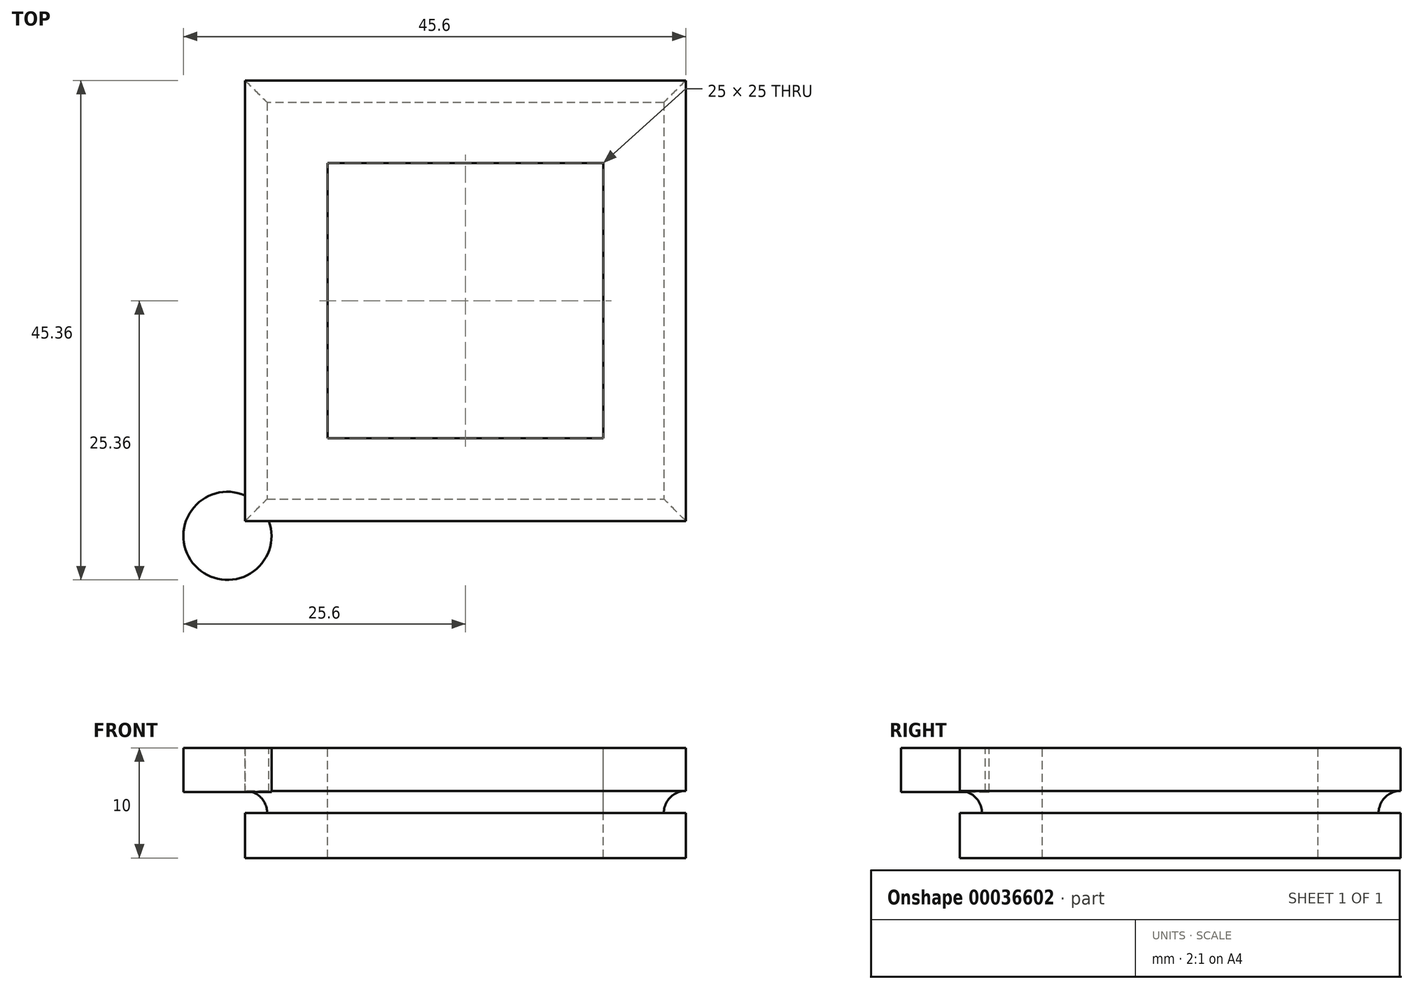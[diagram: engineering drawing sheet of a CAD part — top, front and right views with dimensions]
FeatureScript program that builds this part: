
annotation { "Feature Type Name" : "Feature", "Feature Type Description" : "" }
export const myFeature = defineFeature(function(context is Context, id is Id, definition is map)
    precondition{}
    {
        {
            var Q0;
            Q0=qCreatedBy(makeId("Top.planeOp"),FACE);
            var sketch = newSketch(context, id + "F0", { "sketchPlane" : qUnion([Q0])});
            skLineSegment(sketch, "E0.rect.bottom", {"start": v(-20, -20) * mm, "end": v(20, -20) * mm});
            skLineSegment(sketch, "E0.rect.top", {"start": v(-20, 20) * mm, "end": v(20, 20) * mm});
            skLineSegment(sketch, "E0.rect.left", {"start": v(-20, -20) * mm, "end": v(-20, 20) * mm});
            skLineSegment(sketch, "E0.rect.right", {"start": v(20, -20) * mm, "end": v(20, 20) * mm});
            skPoint(sketch, "E0.rect.middle", {"position": v(0, 0) * mm});
            skSolve(sketch);
        }
        {
            var Q0;
            Q0=makeQuery(id+"F0.imprint","IMPRINT",FACE,{"disambiguationData":[TD([[makeQuery(id+"F0.imprint","IMPRINT",EDGE,{"derivedFrom":sQuery(id+"F0.wireOp",EDGE,"E0.rect.bottom")}),1.0]])]});
            extrude(context, id + "F1", {"entities" : qUnion([Q0]), "depth" : 10 * mm});
        }
        {
            var Q0;
            Q0=makeQuery(id+"F1.opExtrude","CAP_FACE",FACE,{"disambiguationData":[OSD([sQuery(id+"F0.wireOp",EDGE,"E0.rect.bottom"),sQuery(id+"F0.wireOp",EDGE,"E0.rect.top"),sQuery(id+"F0.wireOp",EDGE,"E0.rect.left"),sQuery(id+"F0.wireOp",EDGE,"E0.rect.right")])],"isStart":false});
            var sketch = newSketch(context, id + "F2", { "sketchPlane" : qUnion([Q0])});
            skLineSegment(sketch, "E1.rect.bottom", {"start": v(-12.5, 12.5) * mm, "end": v(12.5, 12.5) * mm});
            skLineSegment(sketch, "E1.rect.top", {"start": v(-12.5, -12.5) * mm, "end": v(12.5, -12.5) * mm});
            skLineSegment(sketch, "E1.rect.left", {"start": v(-12.5, 12.5) * mm, "end": v(-12.5, -12.5) * mm});
            skLineSegment(sketch, "E1.rect.right", {"start": v(12.5, 12.5) * mm, "end": v(12.5, -12.5) * mm});
            skPoint(sketch, "E1.rect.middle", {"position": v(0, 0) * mm});
            skSolve(sketch);
        }
        {
            var Q0;
            Q0=makeQuery(id+"F2.imprint","IMPRINT",FACE,{"disambiguationData":[TD([[makeQuery(id+"F2.imprint","IMPRINT",EDGE,{"derivedFrom":sQuery(id+"F2.wireOp",EDGE,"E1.rect.bottom")}),-1.0]])]});
            extrude(context, id + "F3", {"entities" : qUnion([Q0]), "operationType" : NewBodyOperationType.REMOVE, "oppositeDirection" : true, "depth" : 10 * mm});
        }
        {
            var Q0;
            Q0=makeQuery(id+"F1.opExtrude","SWEPT_FACE",FACE,{"disambiguationData":[OSD([sQuery(id+"F0.wireOp",EDGE,"E0.rect.bottom")])]});
            var sketch = newSketch(context, id + "F4", { "sketchPlane" : qUnion([Q0])});
            skLineSegment(sketch, "E2.bottom", {"start": v(-20, 6.1) * mm, "end": v(20, 6.1) * mm});
            skLineSegment(sketch, "E2.top", {"start": v(-20, 4.1) * mm, "end": v(20, 4.1) * mm});
            skLineSegment(sketch, "E2.left", {"start": v(-20, 6.1) * mm, "end": v(-20, 4.1) * mm});
            skLineSegment(sketch, "E2.right", {"start": v(20, 6.1) * mm, "end": v(20, 4.1) * mm});
            skSolve(sketch);
        }
        {
            var Q0;
            Q0=makeQuery(id+"F4.imprint","IMPRINT",FACE,{"disambiguationData":[TD([[makeQuery(id+"F4.imprint","IMPRINT",EDGE,{"derivedFrom":sQuery(id+"F4.wireOp",EDGE,"E2.bottom")}),-1.0]])]});
            extrude(context, id + "F5", {"entities" : qUnion([Q0]), "operationType" : NewBodyOperationType.REMOVE, "oppositeDirection" : true, "depth" : 2 * mm});
        }
        {
            var Q0;
            Q0=makeQuery(id+"F1.opExtrude","SWEPT_FACE",FACE,{"disambiguationData":[OSD([sQuery(id+"F0.wireOp",EDGE,"E0.rect.right")])]});
            var sketch = newSketch(context, id + "F6", { "sketchPlane" : qUnion([Q0])});
            skLineSegment(sketch, "E3.bottom", {"start": v(-18, 6.1) * mm, "end": v(20, 6.1) * mm});
            skLineSegment(sketch, "E3.top", {"start": v(-18, 4.1) * mm, "end": v(20, 4.1) * mm});
            skLineSegment(sketch, "E3.left", {"start": v(-18, 6.1) * mm, "end": v(-18, 4.1) * mm});
            skLineSegment(sketch, "E3.right", {"start": v(20, 6.1) * mm, "end": v(20, 4.1) * mm});
            skSolve(sketch);
        }
        {
            var Q0;
            Q0=makeQuery(id+"F6.imprint","IMPRINT",FACE,{"disambiguationData":[TD([[makeQuery(id+"F6.imprint","IMPRINT",EDGE,{"derivedFrom":sQuery(id+"F6.wireOp",EDGE,"E3.bottom")}),-1.0]])]});
            extrude(context, id + "F7", {"entities" : qUnion([Q0]), "operationType" : NewBodyOperationType.REMOVE, "oppositeDirection" : true, "depth" : 2 * mm});
        }
        {
            var Q0;
            Q0=makeQuery(id+"F1.opExtrude","SWEPT_FACE",FACE,{"disambiguationData":[OSD([sQuery(id+"F0.wireOp",EDGE,"E0.rect.top")])]});
            var sketch = newSketch(context, id + "F8", { "sketchPlane" : qUnion([Q0])});
            skLineSegment(sketch, "E4.bottom", {"start": v(-18, 6.1) * mm, "end": v(20, 6.1) * mm});
            skLineSegment(sketch, "E4.top", {"start": v(-18, 4.1) * mm, "end": v(20, 4.1) * mm});
            skLineSegment(sketch, "E4.left", {"start": v(-18, 6.1) * mm, "end": v(-18, 4.1) * mm});
            skLineSegment(sketch, "E4.right", {"start": v(20, 6.1) * mm, "end": v(20, 4.1) * mm});
            skSolve(sketch);
        }
        {
            var Q0;
            {var subQ5=sQuery(id+"F8.wireOp",EDGE,"E4.bottom");Q0=makeQuery(id+"F8.imprint","IMPRINT",FACE,{"disambiguationData":[TD([[makeQuery(id+"F8.imprint","IMPRINT",EDGE,{"derivedFrom":subQ5}),-1.0]])]});}
            extrude(context, id + "F9", {"entities" : qUnion([Q0]), "operationType" : NewBodyOperationType.REMOVE, "oppositeDirection" : true, "depth" : 2 * mm});
        }
        {
            var Q0;
            Q0=makeQuery(id+"F1.opExtrude","SWEPT_FACE",FACE,{"disambiguationData":[OSD([sQuery(id+"F0.wireOp",EDGE,"E0.rect.left")])]});
            var sketch = newSketch(context, id + "F10", { "sketchPlane" : qUnion([Q0])});
            skLineSegment(sketch, "E5.bottom", {"start": v(-18, 6.1) * mm, "end": v(18, 6.1) * mm});
            skLineSegment(sketch, "E5.top", {"start": v(-18, 4.1) * mm, "end": v(18, 4.1) * mm});
            skLineSegment(sketch, "E5.left", {"start": v(-18, 6.1) * mm, "end": v(-18, 4.1) * mm});
            skLineSegment(sketch, "E5.right", {"start": v(18, 6.1) * mm, "end": v(18, 4.1) * mm});
            skSolve(sketch);
        }
        {
            var Q0;
            Q0=makeQuery(id+"F10.imprint","IMPRINT",FACE,{"disambiguationData":[TD([[makeQuery(id+"F10.imprint","IMPRINT",EDGE,{"derivedFrom":sQuery(id+"F10.wireOp",EDGE,"E5.bottom")}),-1.0]])]});
            extrude(context, id + "F11", {"entities" : qUnion([Q0]), "operationType" : NewBodyOperationType.REMOVE, "oppositeDirection" : true, "depth" : 2 * mm});
        }
        {
            var Q0;
            Q0=makeQuery(id+"F7.boolean.opBoolean","COPY",EDGE,{"derivedFrom":makeQuery(id+"F7.opExtrude","CAP_EDGE",EDGE,{"disambiguationData":[OSD([sQuery(id+"F6.wireOp",EDGE,"E3.bottom")])],"isStart":false})});
            var Q1;
            Q1=makeQuery(id+"F9.boolean.opBoolean","COPY",EDGE,{"derivedFrom":makeQuery(id+"F9.opExtrude","CAP_EDGE",EDGE,{"disambiguationData":[OSD([sQuery(id+"F8.wireOp",EDGE,"E4.bottom")])],"isStart":false})});
            fillet(context, id + "F12", {"entities" : qUnion([Q0, Q1]), "radius" : 2 * mm, "tangentPropagation" : true, "allowEdgeOverflow" : false});
        }
        {
            var Q0;
            Q0=makeQuery(id+"F5.boolean.opBoolean","COPY",EDGE,{"derivedFrom":makeQuery(id+"F5.opExtrude","CAP_EDGE",EDGE,{"disambiguationData":[OSD([sQuery(id+"F4.wireOp",EDGE,"E2.bottom")])],"isStart":false})});
            var Q1;
            Q1=makeQuery(id+"F11.boolean.opBoolean","COPY",EDGE,{"derivedFrom":makeQuery(id+"F11.opExtrude","CAP_EDGE",EDGE,{"disambiguationData":[OSD([sQuery(id+"F10.wireOp",EDGE,"E5.bottom")])],"isStart":false})});
            fillet(context, id + "F13", {"entities" : qUnion([Q0, Q1]), "radius" : 2 * mm, "tangentPropagation" : true, "allowEdgeOverflow" : false});
        }
        {
            var Q0;
            Q0=makeQuery(id+"F1.opExtrude","CAP_FACE",FACE,{"disambiguationData":[OSD([sQuery(id+"F0.wireOp",EDGE,"E0.rect.bottom"),sQuery(id+"F0.wireOp",EDGE,"E0.rect.top"),sQuery(id+"F0.wireOp",EDGE,"E0.rect.left"),sQuery(id+"F0.wireOp",EDGE,"E0.rect.right")])],"isStart":false});
            var sketch = newSketch(context, id + "F14", { "sketchPlane" : qUnion([Q0])});
            skSolve(sketch);
        }
        {
            var Q0;
            Q0=makeQuery(id+"F14.imprint","IMPRINT",FACE,{"disambiguationData":[TD([[makeQuery(id+"F14.imprint","IMPRINT",EDGE,{"derivedFrom":makeQuery(id+"F1.opExtrude","CAP_EDGE",EDGE,{"disambiguationData":[OSD([sQuery(id+"F0.wireOp",EDGE,"E0.rect.bottom")])],"isStart":false})}),1.0]])]});
            var sketch = newSketch(context, id + "F15", { "sketchPlane" : qUnion([Q0])});
            skCircle(sketch, "E6", {"center": v(-21.6, -21.36) * mm, "radius": 4 * mm});
            skPoint(sketch, "E6.first.point", {"position": v(-17.79, -20.15) * mm});
            skPoint(sketch, "E6.second.point", {"position": v(-20.06, -17.67) * mm});
            skPoint(sketch, "E6.third.point", {"position": v(-25.57, -21.88) * mm});
            skSolve(sketch);
        }
        {
            var Q0;
            {var subQ1=sQuery(id+"F15.wireOp",EDGE,"E6");var subQ3=makeQuery(id+"F14.imprint","IMPRINT",EDGE,{"derivedFrom":makeQuery(id+"F1.opExtrude","CAP_EDGE",EDGE,{"disambiguationData":[OSD([sQuery(id+"F0.wireOp",EDGE,"E0.rect.bottom")])],"isStart":false})});var subQ5=makeQuery(id+"F15.imprint","INTERSECT",VERTEX,{"derivedFrom":[subQ3,subQ1]});Q0=makeQuery(id+"F15.imprint","IMPRINT",FACE,{"disambiguationData":[TD([[makeQuery(id+"F15.imprint","IMPRINT",EDGE,{"disambiguationData":[TD([[subQ5,1.0]])],"derivedFrom":subQ1}),1.0]])]});}
            extrude(context, id + "F16", {"entities" : qUnion([Q0]), "oppositeDirection" : true, "depth" : 4 * mm});
        }
    });
